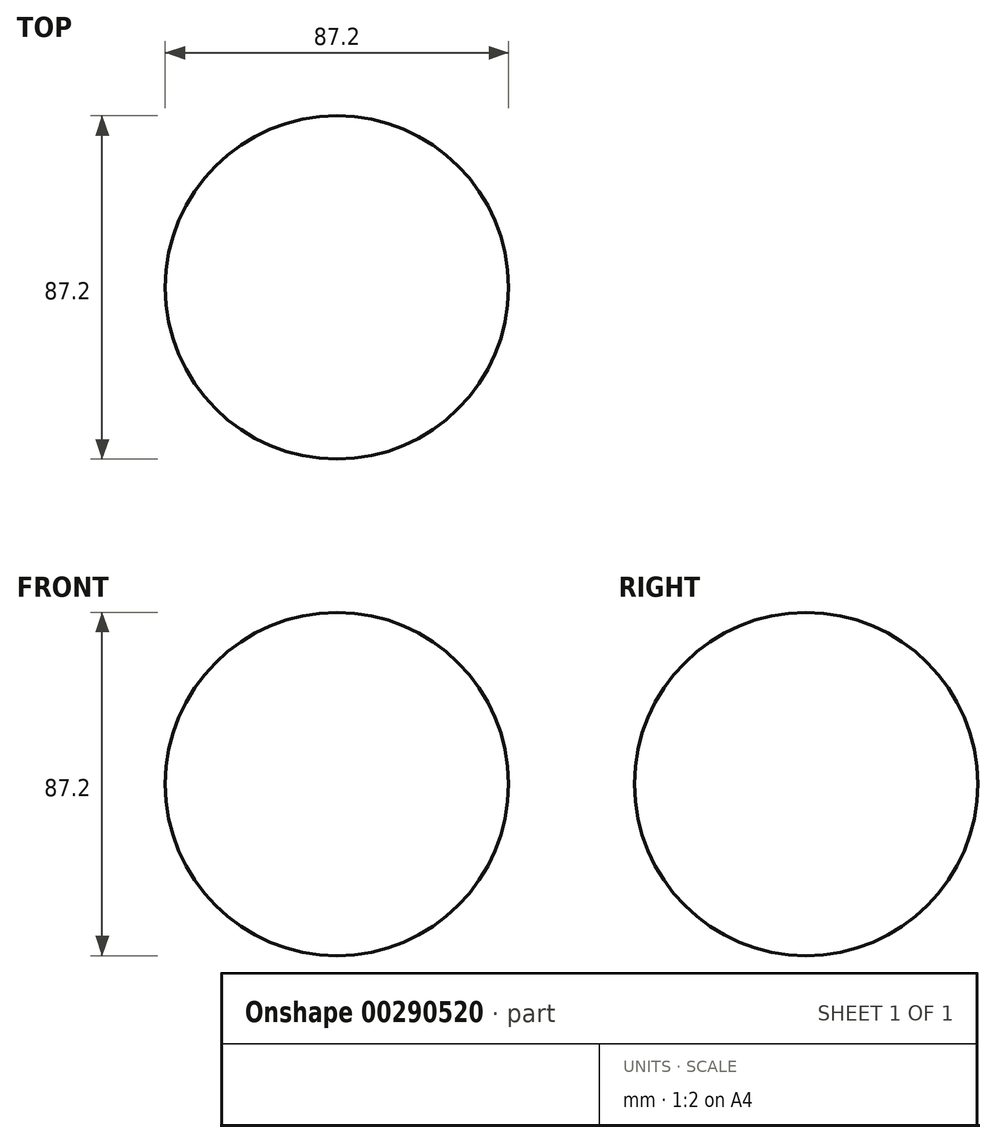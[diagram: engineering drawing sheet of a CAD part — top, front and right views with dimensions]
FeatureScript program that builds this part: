
annotation { "Feature Type Name" : "Feature", "Feature Type Description" : "" }
export const myFeature = defineFeature(function(context is Context, id is Id, definition is map)
    precondition{}
    {
        {
            var Q0;
            Q0=qCreatedBy(makeId("Front.planeOp"),FACE);
            var sketch = newSketch(context, id + "F0", { "sketchPlane" : qUnion([Q0])});
            skLineSegment(sketch, "E0", {"start": v(0, 43.6) * mm, "end": v(0, -43.6) * mm});
            skArc(sketch, "E1", {"start": v(-43.6, 0) * mm, "mid": v(-30.83, 30.83) * mm, "end": v(0, 43.6) * mm});
            skArc(sketch, "E2", {"start": v(-43.6, 0) * mm, "mid": v(-30.83, -30.83) * mm, "end": v(0, -43.6) * mm});
            skSolve(sketch);
        }
        {
            var Q0;
            Q0=makeQuery(id+"F0.imprint","IMPRINT",FACE,{"disambiguationData":[TD([[makeQuery(id+"F0.imprint","IMPRINT",EDGE,{"derivedFrom":sQuery(id+"F0.wireOp",EDGE,"E0")}),-1.0]])]});
            var Q1;
            Q1=sQuery(id+"F0.wireOp",EDGE,"E0");
            revolve(context, id + "F1", {"entities" : qUnion([Q0]), "axis" : qUnion([Q1]), "revolveType" : RevolveType.FULL});
        }
        {
            var Q0;
            Q0=qCreatedBy(makeId("Top.planeOp"),FACE);
            var sketch = newSketch(context, id + "F2", { "sketchPlane" : qUnion([Q0])});
            skCircle(sketch, "E3", {"center": v(14.7, -13.43) * mm, "radius": 5.2 * mm});
            skSolve(sketch);
        }
        {
            var Q0;
            Q0=sQuery(id+"F2.wireOp",EDGE,"E3");
            extrude(context, id + "F3", {"bodyType" : ToolBodyType.SURFACE, "surfaceEntities" : qUnion([Q0]), "depth" : 63.5 * mm});
        }
    });
